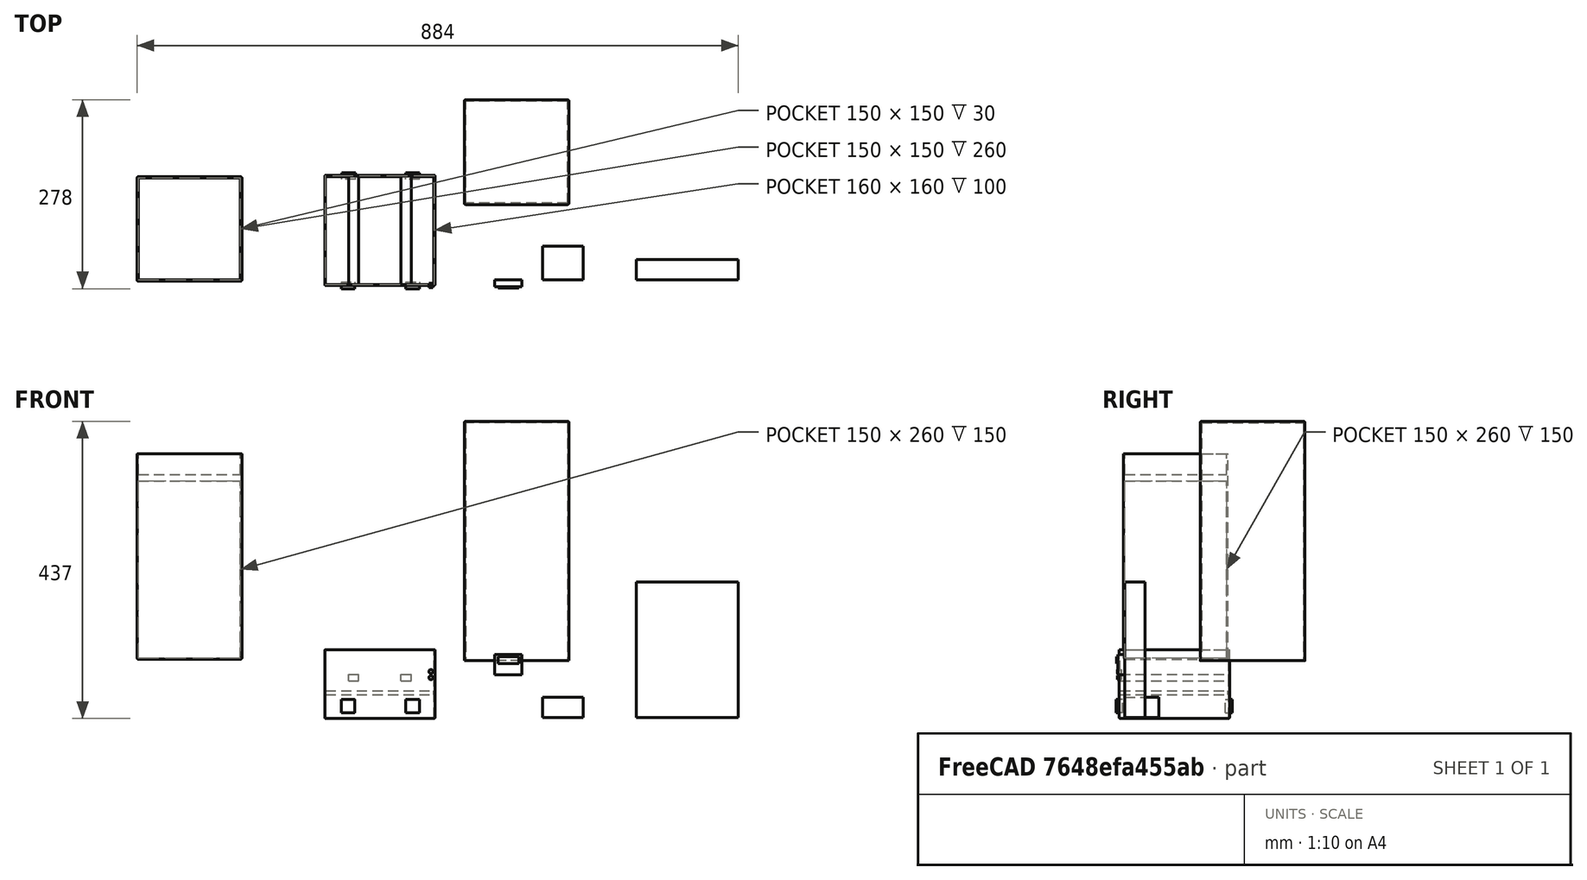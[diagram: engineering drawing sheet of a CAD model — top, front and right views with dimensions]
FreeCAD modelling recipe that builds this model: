
FCSTD DOCUMENT  (FreeCAD 0.20R29177 +233 (Git))
Label: grow
License: All rights reserved
LicenseURL: http://en.wikipedia.org/wiki/All_rights_reserved
objects: Part::Box×19, Part::MultiFuse×6, Part::Thickness×3, Part::Cylinder×2
note: 30 computed .brp shape members not serialized (recipe doc carries the construction recipe); baked Part::Feature solids carry a one-line shape summary decoded from their .brp

FEATURE [Part::Box] Box  label="Cube"
  AttacherType = Attacher::AttachEngine3D
  Height = 300
  Length = 150
  Width = 150
FEATURE [Part::Thickness] Thickness  label="Grow bag"
  Faces = -> Box [Face6]
  Intersection = false
  Join = 0
  Mode = 0
  SelfIntersection = false
  Value = 2
FEATURE [Part::Box] Box001  label="Cube001"
  AttacherType = Attacher::AttachEngine3D
  Height = 100
  Length = 160
  Placement = pos=(187,-7,0) rot=(0,0,1;0rad)
  Width = 160
FEATURE [Part::Thickness] Thickness001  label="Heat try"
  Faces = -> Box001 [Face6]
  Intersection = false
  Join = 0
  Mode = 0
  SelfIntersection = false
  Value = 1
FEATURE [Part::Box] Box002  label="peltiers"
  AttacherType = Attacher::AttachEngine3D
  Height = 5
  Length = 20
  Placement = pos=(210,-19,7) rot=(1,0,0;1.5708rad)
  Width = 20
FEATURE [Part::Box] Box006  label="Charge conroller"
  AttacherType = Attacher::AttachEngine3D
  Height = 10
  Length = 40
  Placement = pos=(244,6.9e-15,31) rot=(1,0,0;1.5708rad)
  Width = 30
FEATURE [Part::Box] Box007  label="Display"
  AttacherType = Attacher::AttachEngine3D
  Height = 8
  Length = 30
  Placement = pos=(249,-4,48) rot=(1,0,0;1.5708rad)
  Width = 10
FEATURE [Part::Box] Box008  label="Dirt"
  AttacherType = Attacher::AttachEngine3D
  Height = 10
  Length = 150
  Placement = pos=(0,0,260) rot=(0,0,1;0rad)
  Width = 150
FEATURE [Part::MultiFuse] Fusion  label="Charge controller"
  Placement = pos=(192,0,32) rot=(0,0,1;0rad)
  Shapes = -> [Box007,Box006]
FEATURE [Part::Cylinder] Cylinder  label="On \ Off"
  Angle = 360
  AttacherType = Attacher::AttachEngine3D
  FirstAngle = 0
  Height = 6
  Placement = pos=(342,-5,68) rot=(1,0,0;1.5708rad)
  Radius = 3
  SecondAngle = 0
FEATURE [Part::Cylinder] Cylinder001  label="On \ Off001"
  Angle = 360
  AttacherType = Attacher::AttachEngine3D
  FirstAngle = 0
  Height = 6
  Placement = pos=(342,-5,59) rot=(1,0,0;1.5708rad)
  Radius = 3
  SecondAngle = 0
FEATURE [Part::Box] Box009  label="Water or air heat gap"
  AttacherType = Attacher::AttachEngine3D
  Height = 6
  Length = 159
  Placement = pos=(187,-7,34) rot=(0,0,1;0rad)
  Width = 159
FEATURE [Part::Box] Box010  label="peltiers001"
  AttacherType = Attacher::AttachEngine3D
  Height = 5
  Length = 20
  Placement = pos=(210,-14,7) rot=(1,0,0;1.5708rad)
  Width = 20
FEATURE [Part::MultiFuse] Fusion001  label="peltiers002"
  Placement = pos=(0,11,0) rot=(0,0,1;0rad)
  Shapes = -> [Box010,Box002]
FEATURE [Part::Box] Box011  label="peltiers003"
  AttacherType = Attacher::AttachEngine3D
  Height = 5
  Length = 20
  Placement = pos=(210,-19,7) rot=(1,0,0;1.5708rad)
  Width = 20
FEATURE [Part::Box] Box012  label="peltiers004"
  AttacherType = Attacher::AttachEngine3D
  Height = 5
  Length = 20
  Placement = pos=(210,-14,7) rot=(1,0,0;1.5708rad)
  Width = 20
FEATURE [Part::MultiFuse] Fusion002  label="peltiers005"
  Placement = pos=(95,11,0) rot=(0,0,1;0rad)
  Shapes = -> [Box012,Box011]
FEATURE [Part::Box] Box013  label="peltiers006"
  AttacherType = Attacher::AttachEngine3D
  Height = 5
  Length = 20
  Placement = pos=(210,-19,7) rot=(1,0,0;1.5708rad)
  Width = 20
FEATURE [Part::Box] Box014  label="peltiers007"
  AttacherType = Attacher::AttachEngine3D
  Height = 5
  Length = 20
  Placement = pos=(210,-14,7) rot=(1,0,0;1.5708rad)
  Width = 20
FEATURE [Part::MultiFuse] Fusion003  label="peltiers008"
  Placement = pos=(441,134,0) rot=(0,0,1;3.14159rad)
  Shapes = -> [Box014,Box013]
FEATURE [Part::Box] Box015  label="peltiers009"
  AttacherType = Attacher::AttachEngine3D
  Height = 5
  Length = 20
  Placement = pos=(210,-19,7) rot=(1,0,0;1.5708rad)
  Width = 20
FEATURE [Part::Box] Box016  label="peltiers010"
  AttacherType = Attacher::AttachEngine3D
  Height = 5
  Length = 20
  Placement = pos=(210,-14,7) rot=(1,0,0;1.5708rad)
  Width = 20
FEATURE [Part::MultiFuse] Fusion004  label="peltiers011"
  Placement = pos=(535,134,0) rot=(0,0,1;3.14159rad)
  Shapes = -> [Box016,Box015]
FEATURE [Part::Box] Box017  label="Shelf"
  AttacherType = Attacher::AttachEngine3D
  Height = 10
  Length = 15
  Placement = pos=(221,-7,54) rot=(0,0,1;0rad)
  Width = 160
FEATURE [Part::Box] Box018  label="Shelf001"
  AttacherType = Attacher::AttachEngine3D
  Height = 10
  Length = 15
  Placement = pos=(298,-7,54) rot=(0,0,1;0rad)
  Width = 160
FEATURE [Part::Box] Box019  label="Power cell"
  AttacherType = Attacher::AttachEngine3D
  Height = 30
  Length = 60
  Placement = pos=(506,0,0) rot=(0,0,1;0rad)
  Width = 50
FEATURE [Part::Box] Box020  label="Solar panel"
  AttacherType = Attacher::AttachEngine3D
  Height = 200
  Length = 150
  Placement = pos=(644,0,0) rot=(0,0,1;0rad)
  Width = 30
FEATURE [Part::Box] Box021  label="Cube002"
  AttacherType = Attacher::AttachEngine3D
  Height = 350
  Length = 150
  Width = 150
FEATURE [Part::Thickness] Thickness002  label="Cover"
  Faces = -> Box021 [Face6]
  Intersection = false
  Join = 0
  Mode = 0
  Placement = pos=(543,113,434) rot=(0,1,0;3.14159rad)
  SelfIntersection = false
  Value = 2
FEATURE [Part::MultiFuse] Fusion005  label="Grow bag001"
  Placement = pos=(-88,0,88) rot=(0,0,1;0rad)
  Shapes = -> [Thickness,Box008]
